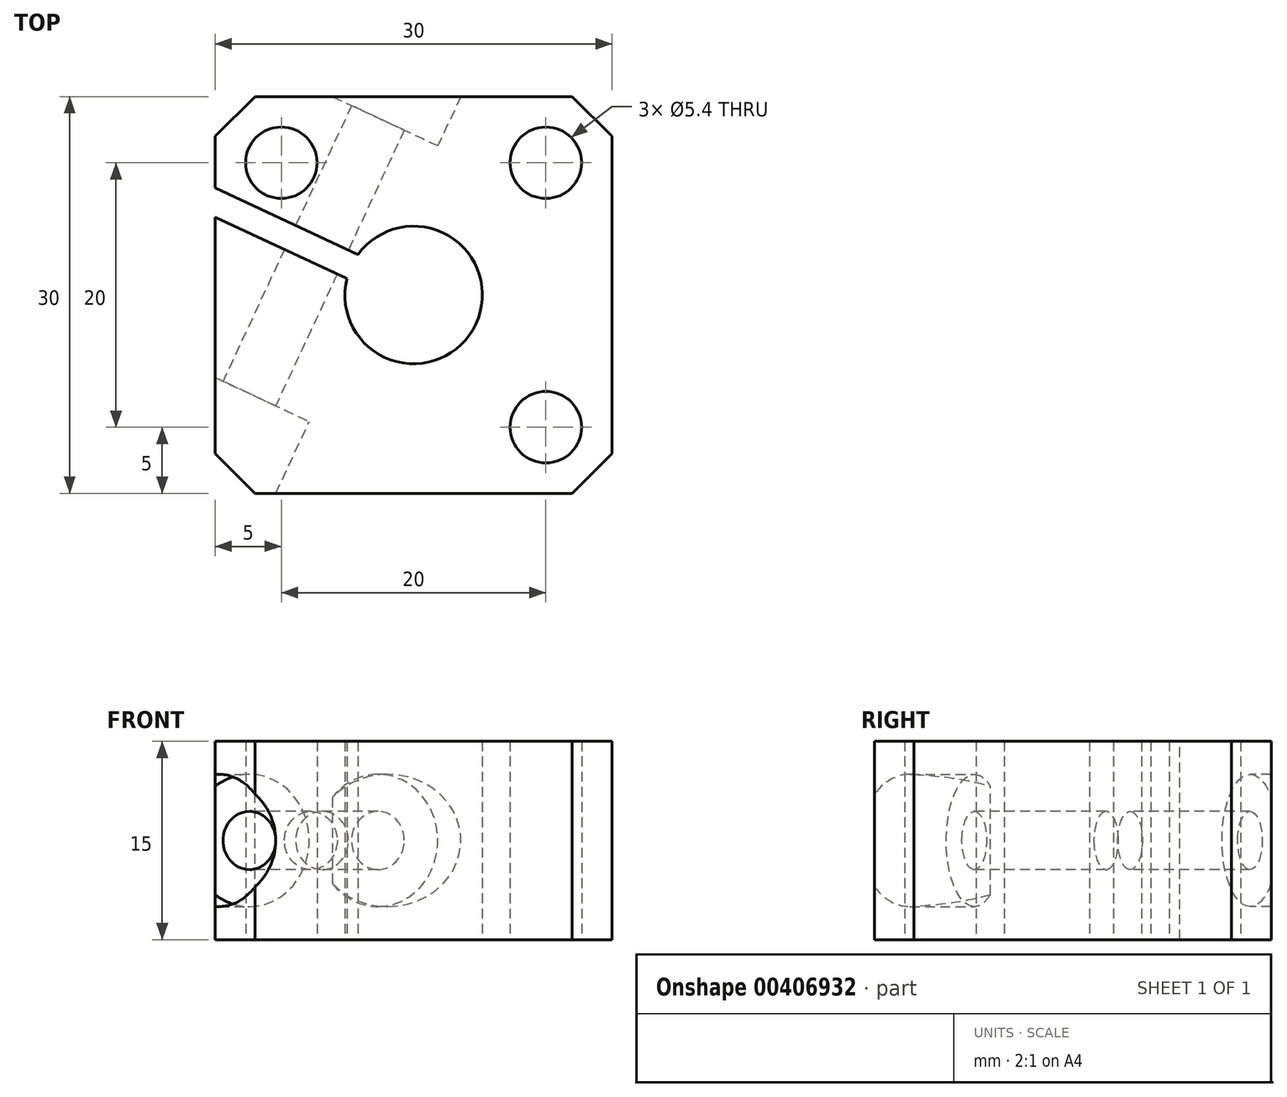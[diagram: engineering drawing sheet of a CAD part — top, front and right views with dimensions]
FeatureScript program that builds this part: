
annotation { "Feature Type Name" : "Feature", "Feature Type Description" : "" }
export const myFeature = defineFeature(function(context is Context, id is Id, definition is map)
    precondition{}
    {
        {
            var Q0;
            Q0=qCreatedBy(makeId("Top.planeOp"),FACE);
            var sketch = newSketch(context, id + "F0", { "sketchPlane" : qUnion([Q0])});
            skCircle(sketch, "E0", {"center": v(0, 0) * mm, "radius": 5.2 * mm});
            skLineSegment(sketch, "E1.bottom", {"start": v(15, -15) * mm, "end": v(-15, -15) * mm});
            skLineSegment(sketch, "E1.top", {"start": v(15, 15) * mm, "end": v(-15, 15) * mm});
            skLineSegment(sketch, "E1.left", {"start": v(15, -15) * mm, "end": v(15, 15) * mm});
            skLineSegment(sketch, "E1.right", {"start": v(-15, -15) * mm, "end": v(-15, 15) * mm});
            skLineSegment(sketch, "E2.bottom", {"start": v(10, -10) * mm, "end": v(-10, -10) * mm, "construction": true});
            skLineSegment(sketch, "E2.top", {"start": v(10, 10) * mm, "end": v(-10, 10) * mm, "construction": true});
            skLineSegment(sketch, "E2.left", {"start": v(10, -10) * mm, "end": v(10, 10) * mm, "construction": true});
            skLineSegment(sketch, "E2.right", {"start": v(-10, -10) * mm, "end": v(-10, 10) * mm, "construction": true});
            skCircle(sketch, "E3", {"center": v(-10, 10) * mm, "radius": 2.7 * mm});
            skCircle(sketch, "E4", {"center": v(10, 10) * mm, "radius": 2.7 * mm});
            skCircle(sketch, "E5", {"center": v(-10, -10) * mm, "radius": 2.7 * mm, "construction": true});
            skCircle(sketch, "E6", {"center": v(10, -10) * mm, "radius": 2.7 * mm});
            skSolve(sketch);
        }
        {
            var Q0;
            Q0 = qSketchRegion(id + "F0", true);
            extrude(context, id + "F1", {"entities" : qUnion([Q0]), "depth" : 15 * mm});
        }
        {
            var Q0;
            Q0=makeQuery(id+"F1.opExtrude","SWEPT_EDGE",EDGE,{"disambiguationData":[OSD([sQuery(id+"F0.wireOp",EDGE,"E1.top"),sQuery(id+"F0.wireOp",EDGE,"E1.left")])]});
            var Q1;
            Q1=makeQuery(id+"F1.opExtrude","SWEPT_EDGE",EDGE,{"disambiguationData":[OSD([sQuery(id+"F0.wireOp",EDGE,"E1.bottom"),sQuery(id+"F0.wireOp",EDGE,"E1.left")])]});
            var Q2;
            Q2=makeQuery(id+"F1.opExtrude","SWEPT_EDGE",EDGE,{"disambiguationData":[OSD([sQuery(id+"F0.wireOp",EDGE,"E1.bottom"),sQuery(id+"F0.wireOp",EDGE,"E1.right")])]});
            var Q3;
            Q3=makeQuery(id+"F1.opExtrude","SWEPT_EDGE",EDGE,{"disambiguationData":[OSD([sQuery(id+"F0.wireOp",EDGE,"E1.top"),sQuery(id+"F0.wireOp",EDGE,"E1.right")])]});
            chamfer(context, id + "F2", {"entities" : qUnion([Q0, Q1, Q2, Q3]), "width" : 3 * mm, "tangentPropagation" : true});
        }
        {
            var Q0;
            Q0=makeQuery(id+"F1.opExtrude","CAP_FACE",FACE,{"disambiguationData":[OSD([sQuery(id+"F0.wireOp",EDGE,"E0"),sQuery(id+"F0.wireOp",EDGE,"E1.bottom"),sQuery(id+"F0.wireOp",EDGE,"E1.top"),sQuery(id+"F0.wireOp",EDGE,"E1.left"),sQuery(id+"F0.wireOp",EDGE,"E1.right"),sQuery(id+"F0.wireOp",EDGE,"E3"),sQuery(id+"F0.wireOp",EDGE,"E4"),sQuery(id+"F0.wireOp",EDGE,"E5"),sQuery(id+"F0.wireOp",EDGE,"E6")])],"isStart":false});
            var sketch = newSketch(context, id + "F3", { "sketchPlane" : qUnion([Q0])});
            skLineSegment(sketch, "E7", {"start": v(0, 0) * mm, "end": v(-27.49, 12.82) * mm, "construction": true});
            skLineSegment(sketch, "E8", {"start": v(-29.77, 13.88) * mm, "end": v(-29.34, 14.79) * mm});
            skLineSegment(sketch, "E9", {"start": v(-29.34, 14.79) * mm, "end": v(-2.15, 2.1) * mm});
            skLineSegment(sketch, "E10", {"start": v(-2.15, 2.1) * mm, "end": v(-3, 0.3) * mm});
            skLineSegment(sketch, "E11", {"start": v(-3, 0.3) * mm, "end": v(-30.19, 12.97) * mm});
            skLineSegment(sketch, "E12", {"start": v(-30.19, 12.97) * mm, "end": v(-29.77, 13.88) * mm});
            skSolve(sketch);
        }
        {
            var Q0;
            Q0 = qSketchRegion(id + "F3", true);
            extrude(context, id + "F4", {"entities" : qUnion([Q0]), "operationType" : NewBodyOperationType.REMOVE, "oppositeDirection" : true, "depth" : 25 * mm});
        }
        {
            var Q0;
            Q0=makeQuery(id+"F4.boolean.opBoolean","COPY",FACE,{"derivedFrom":makeQuery(id+"F4.opExtrude","SWEPT_FACE",FACE,{"disambiguationData":[OSD([sQuery(id+"F3.wireOp",EDGE,"E9")])]})});
            var sketch = newSketch(context, id + "F5", { "sketchPlane" : qUnion([Q0])});
            skLineSegment(sketch, "E13", {"start": v(-11.06, 15) * mm, "end": v(-11.06, 0) * mm, "construction": true});
            skLineSegment(sketch, "E14", {"start": v(-8.1, 15) * mm, "end": v(-8.1, 0) * mm, "construction": true});
            skCircle(sketch, "E15", {"center": v(-8.1, 7.5) * mm, "radius": 2.2 * mm});
            skSolve(sketch);
        }
        {
            var Q0;
            Q0 = qSketchRegion(id + "F5", true);
            extrude(context, id + "F6", {"entities" : qUnion([Q0]), "operationType" : NewBodyOperationType.REMOVE, "endBound" : BoundingType.SYMMETRIC, "oppositeDirection" : true, "depth" : 70 * mm});
        }
        {
            var Q0;
            Q0=makeQuery(id+"F4.boolean.opBoolean","COPY",FACE,{"derivedFrom":makeQuery(id+"F4.opExtrude","SWEPT_FACE",FACE,{"disambiguationData":[OSD([sQuery(id+"F3.wireOp",EDGE,"E9")])]})});
            cPlane(context, id + "F7", {"entities" : qUnion([Q0]), "cplaneType" : CPlaneType.OFFSET, "offset" : 10 * mm, "oppositeDirection" : true, "width" : 150 * mm, "height" : 150 * mm});
        }
        {
            var Q0;
            Q0=qCreatedBy(id+"F7.planeOp",FACE);
            var sketch = newSketch(context, id + "F8", { "sketchPlane" : qUnion([Q0])});
            skCircle(sketch, "E16", {"center": v(-8.1, 7.5) * mm, "radius": 5 * mm});
            skSolve(sketch);
        }
        {
            var Q0;
            Q0 = qSketchRegion(id + "F8", true);
            extrude(context, id + "F9", {"entities" : qUnion([Q0]), "operationType" : NewBodyOperationType.REMOVE, "oppositeDirection" : true, "depth" : 25 * mm});
        }
        {
            var Q0;
            Q0=makeQuery(id+"F4.boolean.opBoolean","COPY",FACE,{"derivedFrom":makeQuery(id+"F4.opExtrude","SWEPT_FACE",FACE,{"disambiguationData":[OSD([sQuery(id+"F3.wireOp",EDGE,"E9")])]})});
            cPlane(context, id + "F10", {"entities" : qUnion([Q0]), "cplaneType" : CPlaneType.OFFSET, "offset" : 13 * mm, "width" : 150 * mm, "height" : 150 * mm});
        }
        {
            var Q0;
            Q0=qCreatedBy(id+"F10.planeOp",FACE);
            var sketch = newSketch(context, id + "F11", { "sketchPlane" : qUnion([Q0])});
            skCircle(sketch, "E17", {"center": v(-8.1, 7.5) * mm, "radius": 5 * mm});
            skSolve(sketch);
        }
        {
            var Q0;
            Q0 = qSketchRegion(id + "F11", true);
            extrude(context, id + "F12", {"entities" : qUnion([Q0]), "operationType" : NewBodyOperationType.REMOVE, "depth" : 25 * mm});
        }
    });
